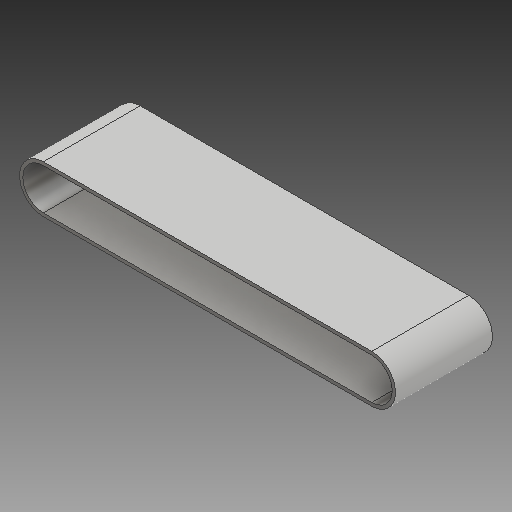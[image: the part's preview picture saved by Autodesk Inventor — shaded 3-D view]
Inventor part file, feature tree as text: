
AUTODESK INVENTOR PART (.ipt)
format: ipt  version: 2019 (Build 230136000, 136)  size: 139,776 bytes
history: native  units: mm
features: extrude x1, sketch x1
ambient origin geometry x8: Origin, YZ Plane, XZ Plane, XY Plane, X Axis, Y Axis, Z Axis, Center Point
bodies: Solid1 (feature_tree)
feature tree (2):
  extrude  "Extrusion1"  Depth=508.0mm
  sketch  "Sketch1"  dims[d0=63.5mm d1=508.0mm d2=73.5mm d3=150.0mm d4=0.0mm]
